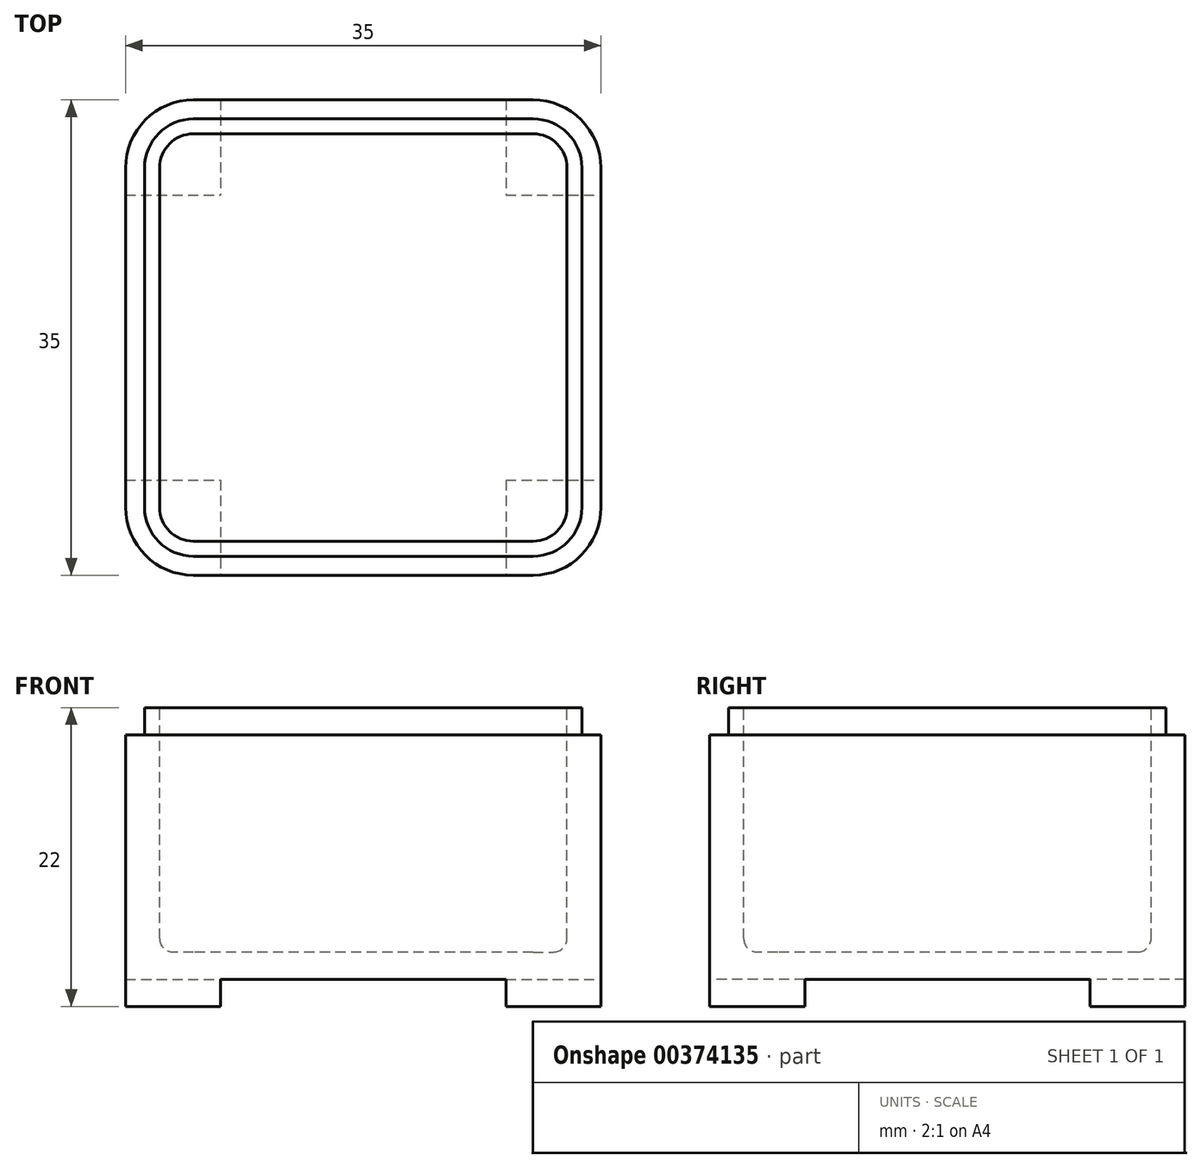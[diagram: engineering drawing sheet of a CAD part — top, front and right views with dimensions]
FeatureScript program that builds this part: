
annotation { "Feature Type Name" : "Feature", "Feature Type Description" : "" }
export const myFeature = defineFeature(function(context is Context, id is Id, definition is map)
    precondition{}
    {
        {
            var Q0;
            Q0=qCreatedBy(makeId("Top.planeOp"),FACE);
            var sketch = newSketch(context, id + "F0", { "sketchPlane" : qUnion([Q0])});
            skLineSegment(sketch, "E0.bottom", {"start": v(17.5, 17.5) * mm, "end": v(-17.5, 17.5) * mm});
            skLineSegment(sketch, "E0.top", {"start": v(17.5, -17.5) * mm, "end": v(-17.5, -17.5) * mm});
            skLineSegment(sketch, "E0.left", {"start": v(17.5, 17.5) * mm, "end": v(17.5, -17.5) * mm});
            skLineSegment(sketch, "E0.right", {"start": v(-17.5, 17.5) * mm, "end": v(-17.5, -17.5) * mm});
            skPoint(sketch, "E0.middle", {"position": v(0, 0) * mm});
            skSolve(sketch);
        }
        {
            var Q0;
            Q0 = qSketchRegion(id + "F0", true);
            extrude(context, id + "F1", {"entities" : qUnion([Q0]), "depth" : 22 * mm, "symmetric" : true});
        }
        {
            var Q0;
            Q0=makeQuery(id+"F1.opExtrude","CAP_FACE",FACE,{"disambiguationData":[OSD([sQuery(id+"F0.wireOp",EDGE,"E0.bottom"),sQuery(id+"F0.wireOp",EDGE,"E0.top"),sQuery(id+"F0.wireOp",EDGE,"E0.left"),sQuery(id+"F0.wireOp",EDGE,"E0.right")])],"isStart":true});
            var sketch = newSketch(context, id + "F2", { "sketchPlane" : qUnion([Q0])});
            skLineSegment(sketch, "E1.bottom", {"start": v(-10.5, -17.5) * mm, "end": v(10.5, -17.5) * mm});
            skLineSegment(sketch, "E1.top", {"start": v(-10.5, 17.5) * mm, "end": v(10.5, 17.5) * mm});
            skLineSegment(sketch, "E1.left", {"start": v(-10.5, -17.5) * mm, "end": v(-10.5, 17.5) * mm});
            skLineSegment(sketch, "E1.right", {"start": v(10.5, -17.5) * mm, "end": v(10.5, 17.5) * mm});
            skLineSegment(sketch, "E2.bottom", {"start": v(-17.5, 10.5) * mm, "end": v(17.5, 10.5) * mm});
            skLineSegment(sketch, "E2.top", {"start": v(-17.5, -10.5) * mm, "end": v(17.5, -10.5) * mm});
            skLineSegment(sketch, "E2.left", {"start": v(-17.5, 10.5) * mm, "end": v(-17.5, -10.5) * mm});
            skLineSegment(sketch, "E2.right", {"start": v(17.5, 10.5) * mm, "end": v(17.5, -10.5) * mm});
            skSolve(sketch);
        }
        {
            var Q0;
            Q0 = qSketchRegion(id + "F2", true);
            extrude(context, id + "F3", {"entities" : qUnion([Q0]), "operationType" : NewBodyOperationType.REMOVE, "oppositeDirection" : true, "depth" : 2 * mm});
        }
        {
            var Q0;
            Q0=makeQuery(id+"F1.opExtrude","CAP_FACE",FACE,{"disambiguationData":[OSD([sQuery(id+"F0.wireOp",EDGE,"E0.bottom"),sQuery(id+"F0.wireOp",EDGE,"E0.top"),sQuery(id+"F0.wireOp",EDGE,"E0.left"),sQuery(id+"F0.wireOp",EDGE,"E0.right")])],"isStart":false});
            var sketch = newSketch(context, id + "F4", { "sketchPlane" : qUnion([Q0])});
            skLineSegment(sketch, "E3.0", {"start": v(-16.1, -16.1) * mm, "end": v(16.1, -16.1) * mm});
            skLineSegment(sketch, "E3.1", {"start": v(-16.1, 16.1) * mm, "end": v(-16.1, -16.1) * mm});
            skLineSegment(sketch, "E3.2", {"start": v(16.1, 16.1) * mm, "end": v(-16.1, 16.1) * mm});
            skLineSegment(sketch, "E3.3", {"start": v(16.1, -16.1) * mm, "end": v(16.1, 16.1) * mm});
            skSolve(sketch);
        }
        {
            var Q0;
            Q0=makeQuery(id+"F4.imprint","IMPRINT",FACE,{"disambiguationData":[TD([[makeQuery(id+"F4.imprint","IMPRINT",EDGE,{"derivedFrom":sQuery(id+"F4.wireOp",EDGE,"E3.0")}),-1.0]])]});
            extrude(context, id + "F5", {"entities" : qUnion([Q0]), "operationType" : NewBodyOperationType.REMOVE, "oppositeDirection" : true, "depth" : 2 * mm});
        }
        {
            var Q0;
            Q0=makeQuery(id+"F1.opExtrude","CAP_FACE",FACE,{"disambiguationData":[OSD([sQuery(id+"F0.wireOp",EDGE,"E0.bottom"),sQuery(id+"F0.wireOp",EDGE,"E0.top"),sQuery(id+"F0.wireOp",EDGE,"E0.left"),sQuery(id+"F0.wireOp",EDGE,"E0.right")])],"isStart":false});
            var sketch = newSketch(context, id + "F6", { "sketchPlane" : qUnion([Q0])});
            skLineSegment(sketch, "E4.bottom", {"start": v(15, 15) * mm, "end": v(-15, 15) * mm});
            skLineSegment(sketch, "E4.top", {"start": v(15, -15) * mm, "end": v(-15, -15) * mm});
            skLineSegment(sketch, "E4.left", {"start": v(15, 15) * mm, "end": v(15, -15) * mm});
            skLineSegment(sketch, "E4.right", {"start": v(-15, 15) * mm, "end": v(-15, -15) * mm});
            skPoint(sketch, "E4.middle", {"position": v(0, 0) * mm});
            skSolve(sketch);
        }
        {
            var Q0;
            Q0=makeQuery(id+"F6.imprint","IMPRINT",FACE,{"disambiguationData":[TD([[makeQuery(id+"F6.imprint","IMPRINT",EDGE,{"derivedFrom":sQuery(id+"F6.wireOp",EDGE,"E4.bottom")}),1.0]])]});
            extrude(context, id + "F7", {"entities" : qUnion([Q0]), "operationType" : NewBodyOperationType.REMOVE, "oppositeDirection" : true, "depth" : 18 * mm});
        }
        {
            var Q0;
            Q0=makeQuery(id+"F7.boolean.opBoolean","COPY",EDGE,{"derivedFrom":makeQuery(id+"F7.opExtrude","CAP_EDGE",EDGE,{"disambiguationData":[OSD([sQuery(id+"F6.wireOp",EDGE,"E4.bottom")])],"isStart":false})});
            var Q1;
            Q1=makeQuery(id+"F7.boolean.opBoolean","COPY",EDGE,{"derivedFrom":makeQuery(id+"F7.opExtrude","CAP_EDGE",EDGE,{"disambiguationData":[OSD([sQuery(id+"F6.wireOp",EDGE,"E4.right")])],"isStart":false})});
            var Q2;
            Q2=makeQuery(id+"F7.boolean.opBoolean","COPY",EDGE,{"derivedFrom":makeQuery(id+"F7.opExtrude","CAP_EDGE",EDGE,{"disambiguationData":[OSD([sQuery(id+"F6.wireOp",EDGE,"E4.top")])],"isStart":false})});
            var Q3;
            Q3=makeQuery(id+"F7.boolean.opBoolean","COPY",EDGE,{"derivedFrom":makeQuery(id+"F7.opExtrude","CAP_EDGE",EDGE,{"disambiguationData":[OSD([sQuery(id+"F6.wireOp",EDGE,"E4.left")])],"isStart":false})});
            fillet(context, id + "F8", {"entities" : qUnion([Q0, Q1, Q2, Q3]), "radius" : 1 * mm, "tangentPropagation" : true, "allowEdgeOverflow" : false});
        }
        {
            var Q0;
            Q0=makeQuery(id+"F7.boolean.opBoolean","COPY",EDGE,{"derivedFrom":makeQuery(id+"F7.opExtrude","SWEPT_EDGE",EDGE,{"disambiguationData":[OSD([sQuery(id+"F6.wireOp",EDGE,"E4.bottom"),sQuery(id+"F6.wireOp",EDGE,"E4.right")])]})});
            var Q1;
            Q1=makeQuery(id+"F7.boolean.opBoolean","COPY",EDGE,{"derivedFrom":makeQuery(id+"F7.opExtrude","SWEPT_EDGE",EDGE,{"disambiguationData":[OSD([sQuery(id+"F6.wireOp",EDGE,"E4.top"),sQuery(id+"F6.wireOp",EDGE,"E4.left")])]})});
            var Q2;
            Q2=makeQuery(id+"F7.boolean.opBoolean","COPY",EDGE,{"derivedFrom":makeQuery(id+"F7.opExtrude","SWEPT_EDGE",EDGE,{"disambiguationData":[OSD([sQuery(id+"F6.wireOp",EDGE,"E4.bottom"),sQuery(id+"F6.wireOp",EDGE,"E4.left")])]})});
            var Q3;
            Q3=makeQuery(id+"F7.boolean.opBoolean","COPY",EDGE,{"derivedFrom":makeQuery(id+"F7.opExtrude","SWEPT_EDGE",EDGE,{"disambiguationData":[OSD([sQuery(id+"F6.wireOp",EDGE,"E4.top"),sQuery(id+"F6.wireOp",EDGE,"E4.right")])]})});
            fillet(context, id + "F9", {"entities" : qUnion([Q0, Q1, Q2, Q3]), "radius" : 2.5 * mm, "tangentPropagation" : true, "allowEdgeOverflow" : false});
        }
        {
            var Q0;
            Q0=makeQuery(id+"F5.boolean.opBoolean","COPY",EDGE,{"derivedFrom":makeQuery(id+"F5.opExtrude","SWEPT_EDGE",EDGE,{"disambiguationData":[OSD([sQuery(id+"F4.wireOp",EDGE,"E3.0"),sQuery(id+"F4.wireOp",EDGE,"E3.1")])]})});
            var Q1;
            Q1=makeQuery(id+"F5.boolean.opBoolean","COPY",EDGE,{"derivedFrom":makeQuery(id+"F5.opExtrude","SWEPT_EDGE",EDGE,{"disambiguationData":[OSD([sQuery(id+"F4.wireOp",EDGE,"E3.0"),sQuery(id+"F4.wireOp",EDGE,"E3.3")])]})});
            var Q2;
            Q2=makeQuery(id+"F5.boolean.opBoolean","COPY",EDGE,{"derivedFrom":makeQuery(id+"F5.opExtrude","SWEPT_EDGE",EDGE,{"disambiguationData":[OSD([sQuery(id+"F4.wireOp",EDGE,"E3.2"),sQuery(id+"F4.wireOp",EDGE,"E3.3")])]})});
            var Q3;
            Q3=makeQuery(id+"F5.boolean.opBoolean","COPY",EDGE,{"derivedFrom":makeQuery(id+"F5.opExtrude","SWEPT_EDGE",EDGE,{"disambiguationData":[OSD([sQuery(id+"F4.wireOp",EDGE,"E3.1"),sQuery(id+"F4.wireOp",EDGE,"E3.2")])]})});
            fillet(context, id + "F10", {"entities" : qUnion([Q0, Q1, Q2, Q3]), "radius" : (5 - 1.4) * mm, "tangentPropagation" : true, "allowEdgeOverflow" : false});
        }
        {
            var Q0;
            Q0=makeQuery(id+"F1.opExtrude","SWEPT_EDGE",EDGE,{"disambiguationData":[OSD([sQuery(id+"F0.wireOp",EDGE,"E0.top"),sQuery(id+"F0.wireOp",EDGE,"E0.right")])]});
            var Q1;
            Q1=makeQuery(id+"F1.opExtrude","SWEPT_EDGE",EDGE,{"disambiguationData":[OSD([sQuery(id+"F0.wireOp",EDGE,"E0.top"),sQuery(id+"F0.wireOp",EDGE,"E0.left")])]});
            var Q2;
            Q2=makeQuery(id+"F1.opExtrude","SWEPT_EDGE",EDGE,{"disambiguationData":[OSD([sQuery(id+"F0.wireOp",EDGE,"E0.bottom"),sQuery(id+"F0.wireOp",EDGE,"E0.left")])]});
            var Q3;
            Q3=makeQuery(id+"F1.opExtrude","SWEPT_EDGE",EDGE,{"disambiguationData":[OSD([sQuery(id+"F0.wireOp",EDGE,"E0.bottom"),sQuery(id+"F0.wireOp",EDGE,"E0.right")])]});
            fillet(context, id + "F11", {"entities" : qUnion([Q0, Q1, Q2, Q3]), "radius" : 5 * mm, "tangentPropagation" : true, "allowEdgeOverflow" : false});
        }
    });
